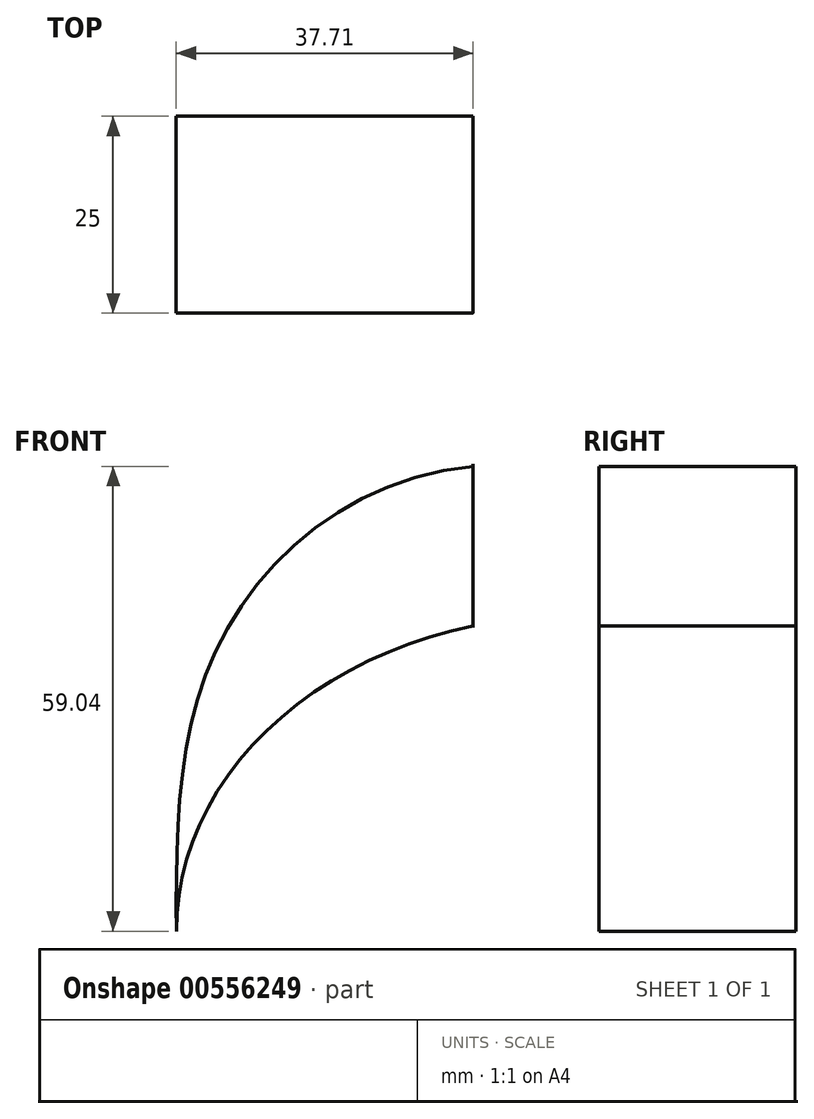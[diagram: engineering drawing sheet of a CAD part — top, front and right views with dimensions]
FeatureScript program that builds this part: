
annotation { "Feature Type Name" : "Feature", "Feature Type Description" : "" }
export const myFeature = defineFeature(function(context is Context, id is Id, definition is map)
    precondition{}
    {
        {
            var Q0;
            Q0=qCreatedBy(makeId("Front.planeOp"),FACE);
            var sketch = newSketch(context, id + "F0", { "sketchPlane" : qUnion([Q0])});
            skEllipse(sketch, "E0", {"center": v(0, 0) * mm, "majorRadius": 50 * mm, "minorRadius": 40 * mm, "majorAxis": v(1, 0)});
            skFitSpline(sketch, "E1", {"points": [v(-50, 0) * mm, v(-44.58, 36.46) * mm, v(-12.3, 59.04) * mm, v(39.13, 36.96) * mm, v(50, 0) * mm], "startDerivative": vector(-0.52, 163.17) * mm, "endDerivative": vector(11.54, -163.32) * mm});
            skFitSpline(sketch, "E2", {"points": [v(-12.3, 59.04) * mm, v(-12.3, 16.27) * mm, v(-9.89, -32.15) * mm, v(-5.91, -39.72) * mm], "startDerivative": vector(0.04, -98.85) * mm, "endDerivative": vector(24.8, -30.5) * mm});
            skSolve(sketch);
        }
        {
            var Q0;
            {var subQ0=sQuery(id+"F0.wireOp",EDGE,"E1");var subQ1=sQuery(id+"F0.wireOp",EDGE,"E0");var subQ2=makeQuery(id+"F0.imprint","INTERSECT",VERTEX,{"disambiguationData":[OD(0.0)],"derivedFrom":[subQ1,subQ0]});Q0=makeQuery(id+"F0.imprint","IMPRINT",FACE,{"disambiguationData":[TD([[makeQuery(id+"F0.imprint","IMPRINT",EDGE,{"disambiguationData":[TD([[subQ2,1.0]])],"derivedFrom":subQ1}),-1.0]])]});}
            extrude(context, id + "F1", {"entities" : qUnion([Q0]), "endBound" : BoundingType.SYMMETRIC, "depth" : 25 * mm, "offsetDistance" : 25 * mm});
        }
    });
